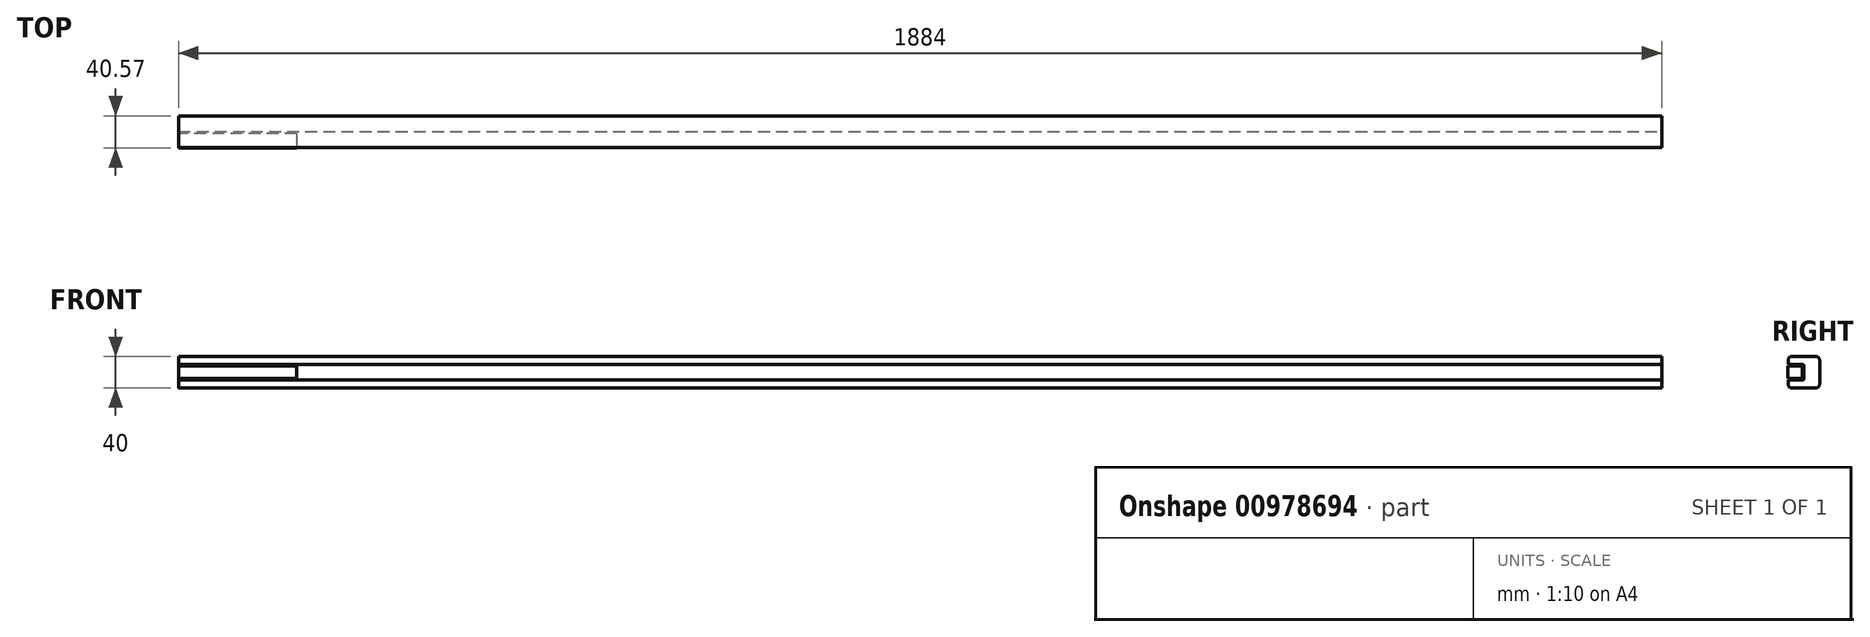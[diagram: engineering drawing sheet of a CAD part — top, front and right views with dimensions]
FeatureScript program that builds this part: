
annotation { "Feature Type Name" : "Feature", "Feature Type Description" : "" }
export const myFeature = defineFeature(function(context is Context, id is Id, definition is map)
    precondition{}
    {
        {
            var Q0;
            Q0=qCreatedBy(makeId("Front.planeOp"),FACE);
            var sketch = newSketch(context, id + "F0", { "sketchPlane" : qUnion([Q0])});
            skLineSegment(sketch, "E0.bottom", {"start": v(-1827.6, 45.39) * mm, "end": v(56.4, 45.39) * mm});
            skLineSegment(sketch, "E0.top", {"start": v(-1827.6, 5.39) * mm, "end": v(56.4, 5.39) * mm});
            skLineSegment(sketch, "E0.left", {"start": v(-1827.6, 45.39) * mm, "end": v(-1827.6, 5.39) * mm});
            skLineSegment(sketch, "E0.right", {"start": v(56.4, 45.39) * mm, "end": v(56.4, 5.39) * mm});
            skSolve(sketch);
        }
        {
            var Q0;
            Q0=makeQuery(id+"F0.imprint","IMPRINT",FACE,{"disambiguationData":[TD([[makeQuery(id+"F0.imprint","IMPRINT",EDGE,{"derivedFrom":sQuery(id+"F0.wireOp",EDGE,"E0.bottom")}),-1.0]])]});
            extrude(context, id + "F1", {"entities" : qUnion([Q0]), "depth" : 40 * mm, "offsetDistance" : 25 * mm});
        }
        {
            var Q0;
            Q0=makeQuery(id+"F1.opExtrude","CAP_EDGE",EDGE,{"disambiguationData":[OSD([sQuery(id+"F0.wireOp",EDGE,"E0.bottom")])],"isStart":false});
            var Q1;
            Q1=makeQuery(id+"F1.opExtrude","CAP_EDGE",EDGE,{"disambiguationData":[OSD([sQuery(id+"F0.wireOp",EDGE,"E0.bottom")])],"isStart":true});
            var Q2;
            Q2=makeQuery(id+"F1.opExtrude","CAP_EDGE",EDGE,{"disambiguationData":[OSD([sQuery(id+"F0.wireOp",EDGE,"E0.top")])],"isStart":false});
            var Q3;
            Q3=makeQuery(id+"F1.opExtrude","CAP_EDGE",EDGE,{"disambiguationData":[OSD([sQuery(id+"F0.wireOp",EDGE,"E0.top")])],"isStart":true});
            fillet(context, id + "F2", {"entities" : qUnion([Q0, Q1, Q2, Q3]), "radius" : 5 * mm, "tangentPropagation" : true, "allowEdgeOverflow" : false});
        }
        {
            var Q0;
            Q0=makeQuery(id+"F1.opExtrude","CAP_FACE",FACE,{"disambiguationData":[OSD([sQuery(id+"F0.wireOp",EDGE,"E0.bottom"),sQuery(id+"F0.wireOp",EDGE,"E0.top"),sQuery(id+"F0.wireOp",EDGE,"E0.left"),sQuery(id+"F0.wireOp",EDGE,"E0.right")])],"isStart":false});
            var sketch = newSketch(context, id + "F3", { "sketchPlane" : qUnion([Q0])});
            skLineSegment(sketch, "E1.bottom", {"start": v(-1827.6, 35.39) * mm, "end": v(56.4, 35.39) * mm});
            skLineSegment(sketch, "E1.top", {"start": v(-1827.6, 15.39) * mm, "end": v(56.4, 15.39) * mm});
            skLineSegment(sketch, "E1.left", {"start": v(-1827.6, 35.39) * mm, "end": v(-1827.6, 15.39) * mm});
            skLineSegment(sketch, "E1.right", {"start": v(56.4, 35.39) * mm, "end": v(56.4, 15.39) * mm});
            skSolve(sketch);
        }
        {
            var Q0;
            Q0=makeQuery(id+"F3.imprint","IMPRINT",FACE,{"disambiguationData":[TD([[makeQuery(id+"F3.imprint","IMPRINT",EDGE,{"derivedFrom":sQuery(id+"F3.wireOp",EDGE,"E1.bottom")}),-1.0]])]});
            extrude(context, id + "F4", {"entities" : qUnion([Q0]), "operationType" : NewBodyOperationType.REMOVE, "oppositeDirection" : true, "depth" : 20 * mm, "offsetDistance" : 25 * mm});
        }
        {
            var Q0;
            Q0=makeQuery(id+"F1.opExtrude","SWEPT_FACE",FACE,{"disambiguationData":[OSD([sQuery(id+"F0.wireOp",EDGE,"E0.left")])]});
            var sketch = newSketch(context, id + "F5", { "sketchPlane" : qUnion([Q0])});
            skLineSegment(sketch, "E2.bottom", {"start": v(22.22, 33.53) * mm, "end": v(40.57, 33.53) * mm});
            skLineSegment(sketch, "E2.top", {"start": v(22.22, 17.19) * mm, "end": v(40.57, 17.19) * mm});
            skLineSegment(sketch, "E2.left", {"start": v(22.22, 33.53) * mm, "end": v(22.22, 17.19) * mm});
            skLineSegment(sketch, "E2.right", {"start": v(40.57, 33.53) * mm, "end": v(40.57, 17.19) * mm});
            skSolve(sketch);
        }
        {
            var Q0;
            Q0=makeQuery(id+"F5.imprint","IMPRINT",FACE,{"disambiguationData":[TD([[makeQuery(id+"F5.imprint","IMPRINT",EDGE,{"derivedFrom":sQuery(id+"F5.wireOp",EDGE,"E2.bottom")}),-1.0]])]});
            extrude(context, id + "F6", {"entities" : qUnion([Q0]), "oppositeDirection" : true, "depth" : 150 * mm, "offsetDistance" : 25 * mm});
        }
        {
            var Q0;
            Q0=makeQuery(id+"F6.opExtrude","SWEPT_EDGE",EDGE,{"disambiguationData":[OSD([sQuery(id+"F5.wireOp",EDGE,"E2.bottom"),sQuery(id+"F5.wireOp",EDGE,"E2.left")])]});
            var Q1;
            Q1=makeQuery(id+"F6.opExtrude","SWEPT_EDGE",EDGE,{"disambiguationData":[OSD([sQuery(id+"F5.wireOp",EDGE,"E2.top"),sQuery(id+"F5.wireOp",EDGE,"E2.left")])]});
            fillet(context, id + "F7", {"entities" : qUnion([Q0, Q1]), "radius" : 2 * mm, "allowEdgeOverflow" : false});
        }
        {
            var Q0;
            Q0=makeQuery(id+"F4.boolean.opBoolean","COPY",EDGE,{"derivedFrom":makeQuery(id+"F4.opExtrude","CAP_EDGE",EDGE,{"disambiguationData":[OSD([sQuery(id+"F3.wireOp",EDGE,"E1.top")])],"isStart":false})});
            var Q1;
            Q1=makeQuery(id+"F4.boolean.opBoolean","COPY",EDGE,{"derivedFrom":makeQuery(id+"F4.opExtrude","CAP_EDGE",EDGE,{"disambiguationData":[OSD([sQuery(id+"F3.wireOp",EDGE,"E1.bottom")])],"isStart":false})});
            fillet(context, id + "F8", {"entities" : qUnion([Q0, Q1]), "radius" : 2 * mm, "tangentPropagation" : true, "allowEdgeOverflow" : false});
        }
    });
